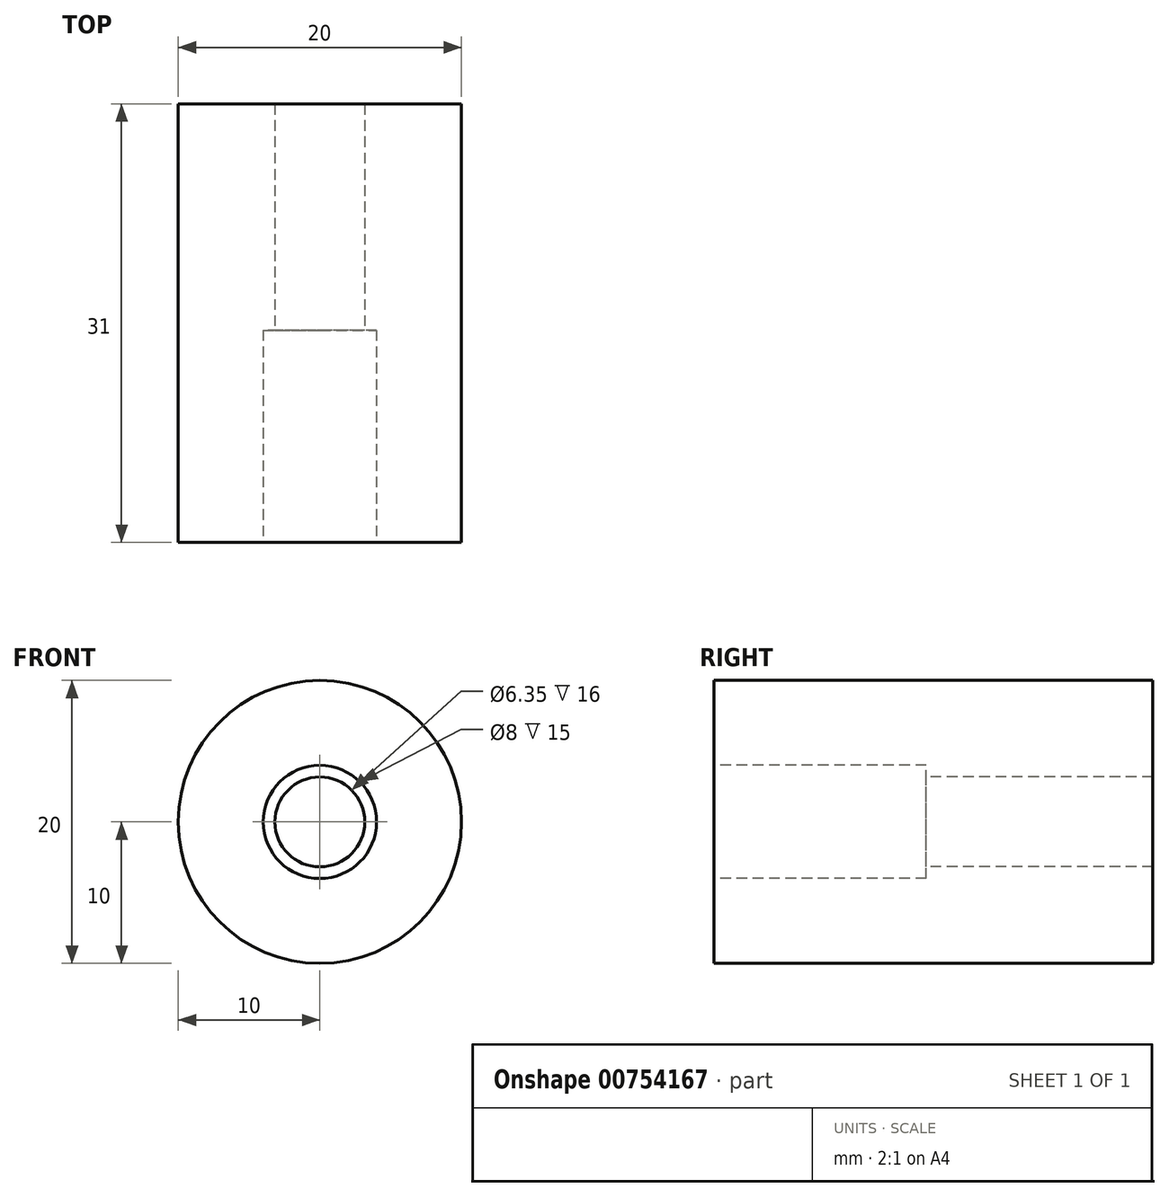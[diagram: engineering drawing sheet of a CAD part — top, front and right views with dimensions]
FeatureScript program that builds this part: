
annotation { "Feature Type Name" : "Feature", "Feature Type Description" : "" }
export const myFeature = defineFeature(function(context is Context, id is Id, definition is map)
    precondition{}
    {
        {
            var Q0;
            Q0=qCreatedBy(makeId("Front.planeOp"),FACE);
            var sketch = newSketch(context, id + "F0", { "sketchPlane" : qUnion([Q0])});
            skCircle(sketch, "E0", {"center": v(0, 0) * mm, "radius": 10 * mm});
            skSolve(sketch);
        }
        {
            var Q0;
            Q0=makeQuery(id+"F0.imprint","IMPRINT",FACE,{"disambiguationData":[TD([[makeQuery(id+"F0.imprint","IMPRINT",EDGE,{"derivedFrom":sQuery(id+"F0.wireOp",EDGE,"E0")}),1.0]])]});
            extrude(context, id + "F1", {"entities" : qUnion([Q0]), "oppositeDirection" : true, "depth" : 31 * mm, "offsetDistance" : 25 * mm});
        }
        {
            var Q0;
            Q0=makeQuery(id+"F1.opExtrude","CAP_FACE",FACE,{"disambiguationData":[OSD([sQuery(id+"F0.wireOp",EDGE,"E0")])],"isStart":true});
            var sketch = newSketch(context, id + "F2", { "sketchPlane" : qUnion([Q0])});
            skCircle(sketch, "E1", {"center": v(0, 0) * mm, "radius": 4 * mm});
            skSolve(sketch);
        }
        {
            var Q0;
            Q0=sQuery(id+"F2.wireOp",VERTEX,"E1.center");
            var Q1;
            Q1=makeQuery(id+"F1.opExtrude","SWEPT_BODY",BODY,{"disambiguationData":[OSD([sQuery(id+"F0.wireOp",EDGE,"E0")])]});
            hole(context, id + "F3", {"style" : HoleStyle.C_BORE, "endStyle" : HoleEndStyle.THROUGH, "holeDiameter" : 6.35 * mm, "cBoreDiameter" : 8 * mm, "cBoreDepth" : 15 * mm, "majorDiameter" : 5 * mm, "isTappedThrough" : true, "tappedDepth" : 12 * mm, "tapClearance" : 3, "locations" : qUnion([Q0]), "scope" : qUnion([Q1])});
        }
    });
